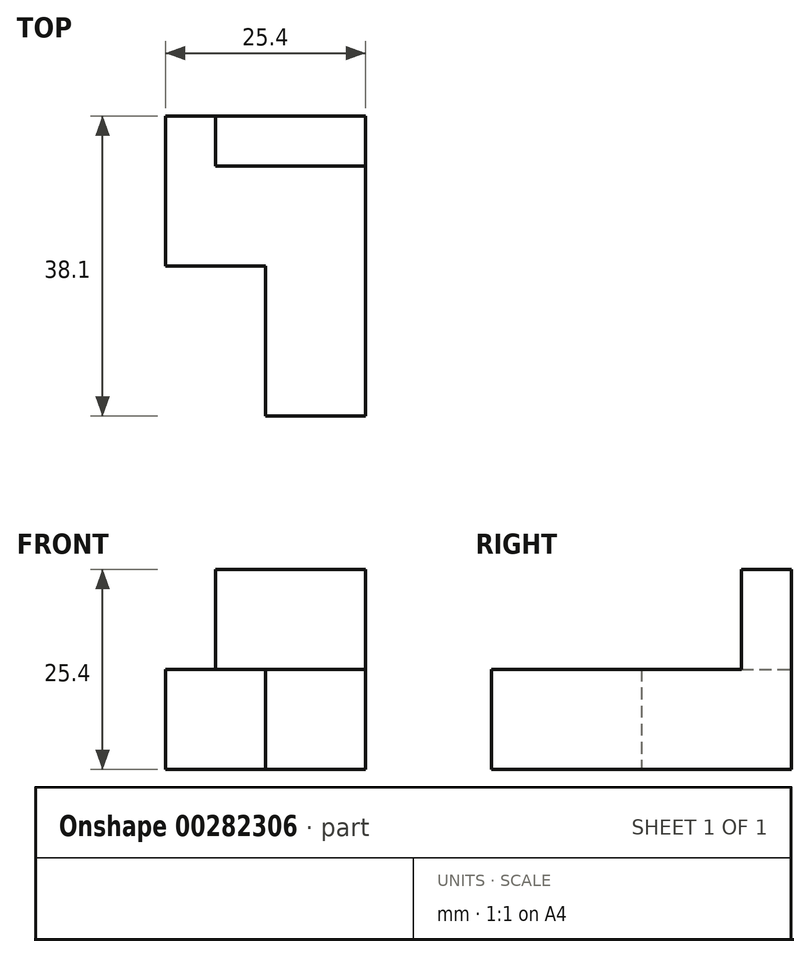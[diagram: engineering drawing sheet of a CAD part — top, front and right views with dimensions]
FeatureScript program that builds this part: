
annotation { "Feature Type Name" : "Feature", "Feature Type Description" : "" }
export const myFeature = defineFeature(function(context is Context, id is Id, definition is map)
    precondition{}
    {
        {
            var Q0;
            Q0=qCreatedBy(makeId("Front.planeOp"),FACE);
            var sketch = newSketch(context, id + "F0", { "sketchPlane" : qUnion([Q0])});
            skLineSegment(sketch, "E0", {"start": v(0, 0) * mm, "end": v(12.7, 0) * mm});
            skLineSegment(sketch, "E1", {"start": v(12.7, 0) * mm, "end": v(12.7, 12.7) * mm});
            skLineSegment(sketch, "E2", {"start": v(12.7, 12.7) * mm, "end": v(0, 12.7) * mm});
            skLineSegment(sketch, "E3", {"start": v(0, 12.7) * mm, "end": v(0, 0) * mm});
            skSolve(sketch);
        }
        {
            var Q0;
            Q0 = qSketchRegion(id + "F0", true);
            extrude(context, id + "F1", {"entities" : qUnion([Q0]), "depth" : 38.1 * mm});
        }
        {
            var Q0;
            Q0=makeQuery(id+"F1.opExtrude","SWEPT_FACE",FACE,{"disambiguationData":[OSD([sQuery(id+"F0.wireOp",EDGE,"E3")])]});
            var sketch = newSketch(context, id + "F2", { "sketchPlane" : qUnion([Q0])});
            skLineSegment(sketch, "E4", {"start": v(0, 12.7) * mm, "end": v(19.05, 12.7) * mm});
            skLineSegment(sketch, "E5", {"start": v(19.05, 12.7) * mm, "end": v(19.05, 0) * mm});
            skLineSegment(sketch, "E6", {"start": v(19.05, 0) * mm, "end": v(0, 0) * mm});
            skLineSegment(sketch, "E7", {"start": v(0, 0) * mm, "end": v(0, 12.7) * mm});
            skSolve(sketch);
        }
        {
            var Q0;
            Q0 = qSketchRegion(id + "F2", true);
            extrude(context, id + "F3", {"entities" : qUnion([Q0]), "operationType" : NewBodyOperationType.ADD, "depth" : 12.7 * mm});
        }
        {
            var Q0;
            Q0=makeQuery(id+"F3.boolean.opBoolean","MERGE",FACE,{"derivedFrom":[makeQuery(id+"F1.opExtrude","SWEPT_FACE",FACE,{"disambiguationData":[OSD([sQuery(id+"F0.wireOp",EDGE,"E2")])]}),makeQuery(id+"F3.opExtrude","SWEPT_FACE",FACE,{"disambiguationData":[OSD([sQuery(id+"F2.wireOp",EDGE,"E4")])]})]});
            var sketch = newSketch(context, id + "F4", { "sketchPlane" : qUnion([Q0])});
            skLineSegment(sketch, "E8", {"start": v(12.7, 0) * mm, "end": v(12.7, -6.35) * mm});
            skLineSegment(sketch, "E9", {"start": v(12.7, -6.35) * mm, "end": v(-6.35, -6.35) * mm});
            skLineSegment(sketch, "E10", {"start": v(-6.35, -6.35) * mm, "end": v(-6.35, 0) * mm});
            skLineSegment(sketch, "E11", {"start": v(-6.35, 0) * mm, "end": v(12.7, 0) * mm});
            skSolve(sketch);
        }
        {
            var Q0;
            Q0=makeQuery(id+"F4.imprint","IMPRINT",FACE,{"disambiguationData":[TD([[makeQuery(id+"F4.imprint","IMPRINT",EDGE,{"derivedFrom":sQuery(id+"F4.wireOp",EDGE,"E8")}),1.0]])]});
            extrude(context, id + "F5", {"entities" : qUnion([Q0]), "operationType" : NewBodyOperationType.ADD, "depth" : 12.7 * mm});
        }
    });
